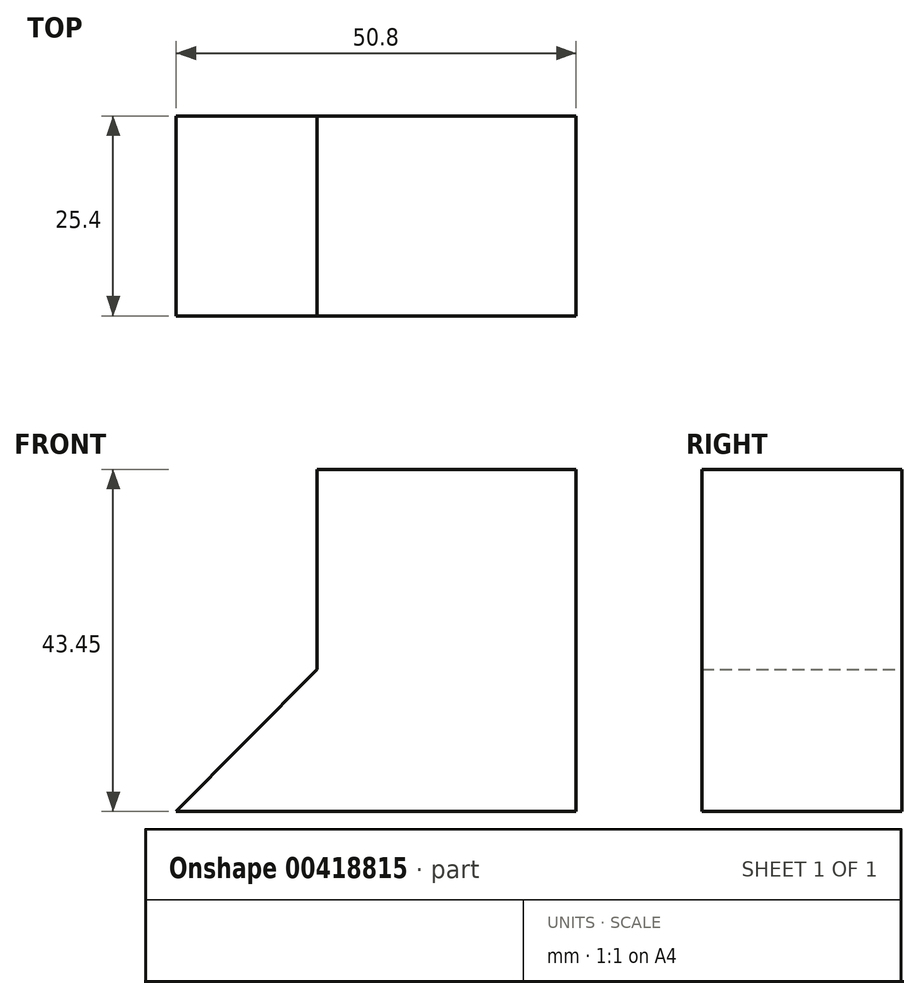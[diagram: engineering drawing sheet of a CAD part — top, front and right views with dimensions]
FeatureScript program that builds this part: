
annotation { "Feature Type Name" : "Feature", "Feature Type Description" : "" }
export const myFeature = defineFeature(function(context is Context, id is Id, definition is map)
    precondition{}
    {
        {
            var Q0;
            Q0=qCreatedBy(makeId("Front.planeOp"),FACE);
            var sketch = newSketch(context, id + "F0", { "sketchPlane" : qUnion([Q0])});
            skLineSegment(sketch, "E0", {"start": v(0, 0) * mm, "end": v(-50.8, 0) * mm});
            skLineSegment(sketch, "E1", {"start": v(-50.8, 0) * mm, "end": v(-32.92, 18.05) * mm});
            skLineSegment(sketch, "E2", {"start": v(-32.92, 18.05) * mm, "end": v(-32.92, 43.45) * mm});
            skLineSegment(sketch, "E3", {"start": v(-32.92, 43.45) * mm, "end": v(0, 43.45) * mm});
            skLineSegment(sketch, "E4", {"start": v(0, 43.45) * mm, "end": v(0, 0) * mm});
            skSolve(sketch);
        }
        {
            var Q0;
            Q0=makeQuery(id+"F0.imprint","IMPRINT",FACE,{"disambiguationData":[TD([[makeQuery(id+"F0.imprint","IMPRINT",EDGE,{"derivedFrom":sQuery(id+"F0.wireOp",EDGE,"E0")}),-1.0]])]});
            extrude(context, id + "F1", {"entities" : qUnion([Q0]), "depth" : 25.4 * mm});
        }
    });
